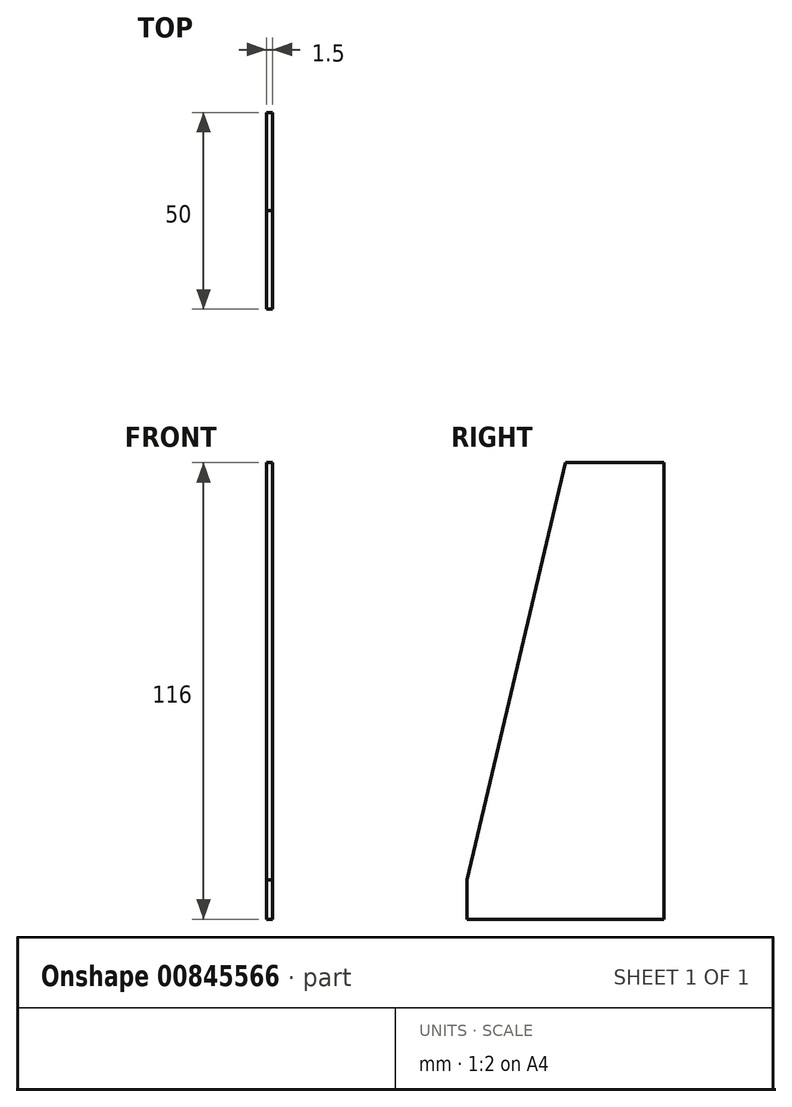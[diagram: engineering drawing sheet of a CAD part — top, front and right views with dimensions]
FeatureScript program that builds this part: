
annotation { "Feature Type Name" : "Feature", "Feature Type Description" : "" }
export const myFeature = defineFeature(function(context is Context, id is Id, definition is map)
    precondition{}
    {
        {
            var Q0;
            Q0=qCreatedBy(makeId("Right.planeOp"),FACE);
            var sketch = newSketch(context, id + "F0", { "sketchPlane" : qUnion([Q0])});
            skLineSegment(sketch, "E0", {"start": v(-33.7, -73.43) * mm, "end": v(16.3, -73.43) * mm});
            skLineSegment(sketch, "E1", {"start": v(16.3, -73.43) * mm, "end": v(16.3, 42.57) * mm});
            skLineSegment(sketch, "E2", {"start": v(16.3, 42.57) * mm, "end": v(-8.7, 42.57) * mm});
            skLineSegment(sketch, "E3", {"start": v(-33.7, -73.43) * mm, "end": v(-33.7, -63.43) * mm});
            skLineSegment(sketch, "E4", {"start": v(-33.7, -63.43) * mm, "end": v(-8.7, 42.57) * mm});
            skSolve(sketch);
        }
        {
            var Q0;
            Q0=makeQuery(id+"F0.imprint","IMPRINT",FACE,{"disambiguationData":[TD([[makeQuery(id+"F0.imprint","IMPRINT",EDGE,{"derivedFrom":sQuery(id+"F0.wireOp",EDGE,"E0")}),1.0]])]});
            extrude(context, id + "F1", {"entities" : qUnion([Q0]), "depth" : 1.5 * mm, "offsetDistance" : 25 * mm});
        }
    });
